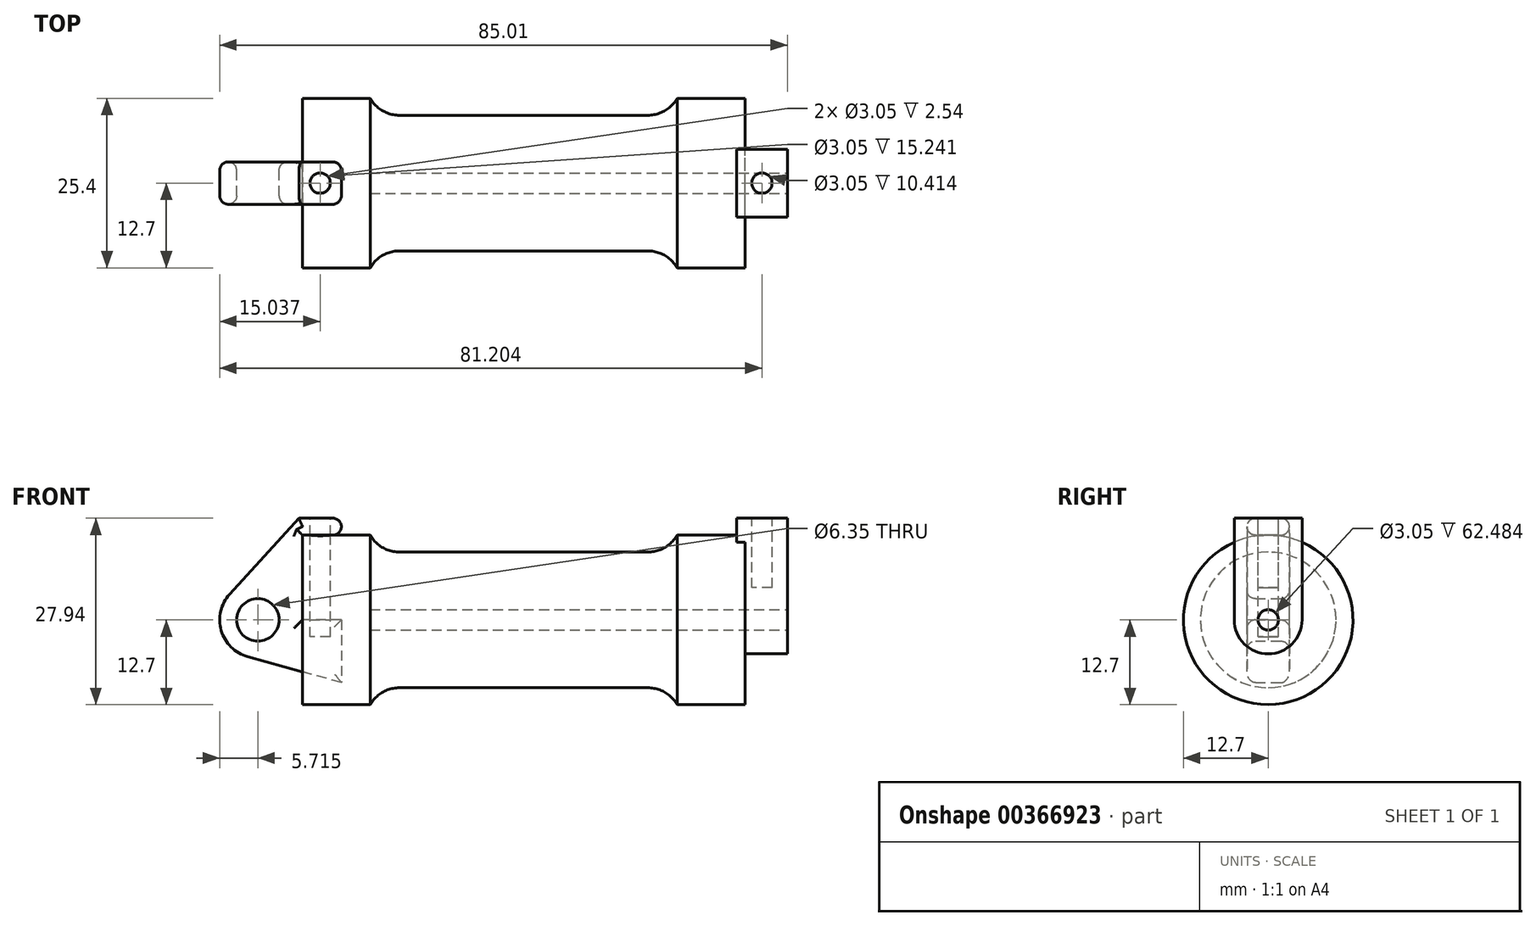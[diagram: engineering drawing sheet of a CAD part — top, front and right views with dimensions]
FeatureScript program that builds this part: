
annotation { "Feature Type Name" : "Feature", "Feature Type Description" : "" }
export const myFeature = defineFeature(function(context is Context, id is Id, definition is map)
    precondition{}
    {
        {
            var Q0;
            Q0=qCreatedBy(makeId("Front.planeOp"),FACE);
            var sketch = newSketch(context, id + "F0", { "sketchPlane" : qUnion([Q0])});
            skLineSegment(sketch, "E0", {"start": v(0, 0) * mm, "end": v(0, 12.7) * mm});
            skLineSegment(sketch, "E1", {"start": v(0, 12.7) * mm, "end": v(10.16, 12.7) * mm});
            skLineSegment(sketch, "E2", {"start": v(10.16, 12.7) * mm, "end": v(10.16, 10.16) * mm});
            skLineSegment(sketch, "E3", {"start": v(10.16, 10.16) * mm, "end": v(56.13, 10.16) * mm});
            skLineSegment(sketch, "E4", {"start": v(56.13, 10.16) * mm, "end": v(56.13, 12.7) * mm});
            skLineSegment(sketch, "E5", {"start": v(56.13, 12.7) * mm, "end": v(66.3, 12.7) * mm});
            skLineSegment(sketch, "E6", {"start": v(66.3, 12.7) * mm, "end": v(66.3, 0) * mm});
            skLineSegment(sketch, "E7", {"start": v(66.3, 0) * mm, "end": v(0, 0) * mm});
            skLineSegment(sketch, "E8", {"start": v(5.84, 15.24) * mm, "end": v(-0.5, 15.24) * mm});
            skLineSegment(sketch, "E9", {"start": v(-0.5, 15.24) * mm, "end": v(-10.88, 3.85) * mm});
            skLineSegment(sketch, "E10", {"start": v(0, 0) * mm, "end": v(-6.65, 0) * mm});
            skCircle(sketch, "E11", {"center": v(-6.65, 0) * mm, "radius": 5.72 * mm});
            skCircle(sketch, "E12", {"center": v(-6.65, 0) * mm, "radius": 3.18 * mm});
            skLineSegment(sketch, "E13", {"start": v(5.84, 15.24) * mm, "end": v(5.84, -9.4) * mm});
            skLineSegment(sketch, "E14", {"start": v(5.84, -9.4) * mm, "end": v(-8.18, -5.5) * mm});
            skSolve(sketch);
        }
        {
            var Q0;
            {var subQ0=sQuery(id+"F0.wireOp",EDGE,"E0");Q0=makeQuery(id+"F0.imprint","IMPRINT",FACE,{"disambiguationData":[TD([[makeQuery(id+"F0.imprint","IMPRINT",EDGE,{"derivedFrom":subQ0}),-1.0]])]});}
            var Q1;
            {var subQ0=sQuery(id+"F0.wireOp",EDGE,"E2");Q1=makeQuery(id+"F0.imprint","IMPRINT",FACE,{"disambiguationData":[TD([[makeQuery(id+"F0.imprint","IMPRINT",EDGE,{"derivedFrom":subQ0}),-1.0]])]});}
            var Q2;
            Q2=sQuery(id+"F0.wireOp",EDGE,"E7");
            revolve(context, id + "F1", {"entities" : qUnion([Q0, Q1]), "axis" : qUnion([Q2]), "revolveType" : RevolveType.FULL});
        }
        {
            var Q0;
            {var subQ1=sQuery(id+"F0.wireOp",EDGE,"E0");Q0=makeQuery(id+"F0.imprint","IMPRINT",FACE,{"disambiguationData":[TD([[makeQuery(id+"F0.imprint","IMPRINT",EDGE,{"derivedFrom":subQ1}),1.0]])]});}
            var Q1;
            {var subQ0=sQuery(id+"F0.wireOp",EDGE,"E14");Q1=makeQuery(id+"F0.imprint","IMPRINT",FACE,{"disambiguationData":[TD([[makeQuery(id+"F0.imprint","IMPRINT",EDGE,{"derivedFrom":subQ0}),-1.0]])]});}
            var Q2;
            {var subQ5=sQuery(id+"F0.wireOp",EDGE,"E12");Q2=makeQuery(id+"F0.imprint","IMPRINT",FACE,{"disambiguationData":[TD([[makeQuery(id+"F0.imprint","IMPRINT",EDGE,{"derivedFrom":subQ5}),-1.0]])]});}
            extrude(context, id + "F2", {"entities" : qUnion([Q0, Q1, Q2]), "endBound" : BoundingType.SYMMETRIC, "depth" : 6.35 * mm});
        }
        {
            var Q0;
            Q0=makeQuery(id+"F1.opRevolve","SWEPT_FACE",FACE,{"disambiguationData":[OSD([sQuery(id+"F0.wireOp",EDGE,"E6")])]});
            var sketch = newSketch(context, id + "F3", { "sketchPlane" : qUnion([Q0])});
            skCircle(sketch, "E15", {"center": v(0, 0) * mm, "radius": 1.52 * mm});
            skCircle(sketch, "E16", {"center": v(0, 0) * mm, "radius": 5.08 * mm});
            skLineSegment(sketch, "E17", {"start": v(5.08, 0) * mm, "end": v(5.08, 15.24) * mm});
            skLineSegment(sketch, "E18", {"start": v(-5.08, 0) * mm, "end": v(-5.08, 15.24) * mm});
            skLineSegment(sketch, "E19", {"start": v(-5.08, 15.24) * mm, "end": v(5.08, 15.24) * mm});
            skSolve(sketch);
        }
        {
            var Q0;
            Q0=makeQuery(id+"F3.imprint","IMPRINT",FACE,{"disambiguationData":[TD([[makeQuery(id+"F3.imprint","IMPRINT",EDGE,{"derivedFrom":sQuery(id+"F3.wireOp",EDGE,"E15")}),1.0]])]});
            var Q1;
            Q1=makeQuery(id+"F1.opRevolve","SWEPT_FACE",FACE,{"disambiguationData":[OSD([sQuery(id+"F0.wireOp",EDGE,"E2")])]});
            extrude(context, id + "F4", {"entities" : qUnion([Q0]), "operationType" : NewBodyOperationType.REMOVE, "endBound" : BoundingType.UP_TO_SURFACE, "oppositeDirection" : true, "endBoundEntityFace" : qUnion([Q1]), "depth" : 25.4 * mm});
        }
        {
            var Q0;
            {var subQ0=sQuery(id+"F3.wireOp",EDGE,"E17");var subQ1=sQuery(id+"F3.wireOp",EDGE,"E16");var subQ2=makeQuery(id+"F3.imprint","INTERSECT",VERTEX,{"derivedFrom":[subQ1,subQ0]});Q0=makeQuery(id+"F3.imprint","IMPRINT",FACE,{"disambiguationData":[TD([[makeQuery(id+"F3.imprint","IMPRINT",EDGE,{"disambiguationData":[TD([[subQ2,-1.0]])],"derivedFrom":subQ1}),-1.0]])]});}
            var Q1;
            Q1=makeQuery(id+"F3.imprint","IMPRINT",FACE,{"disambiguationData":[TD([[makeQuery(id+"F3.imprint","IMPRINT",EDGE,{"derivedFrom":sQuery(id+"F3.wireOp",EDGE,"E15")}),-1.0]])]});
            var Q2;
            {var subQ0=sQuery(id+"F3.wireOp",EDGE,"E19");Q2=makeQuery(id+"F3.imprint","IMPRINT",FACE,{"disambiguationData":[TD([[makeQuery(id+"F3.imprint","IMPRINT",EDGE,{"derivedFrom":subQ0}),-1.0]])]});}
            extrude(context, id + "F5", {"entities" : qUnion([Q0, Q1, Q2]), "operationType" : NewBodyOperationType.ADD, "oppositeDirection" : true, "depth" : 1.27 * mm});
        }
        {
            var Q0;
            {var subQ0=sQuery(id+"F3.wireOp",EDGE,"E17");var subQ1=sQuery(id+"F3.wireOp",EDGE,"E16");var subQ2=makeQuery(id+"F3.imprint","INTERSECT",VERTEX,{"derivedFrom":[subQ1,subQ0]});Q0=makeQuery(id+"F3.imprint","IMPRINT",FACE,{"disambiguationData":[TD([[makeQuery(id+"F3.imprint","IMPRINT",EDGE,{"disambiguationData":[TD([[subQ2,-1.0]])],"derivedFrom":subQ1}),-1.0]])]});}
            var Q1;
            {var subQ0=sQuery(id+"F3.wireOp",EDGE,"E19");Q1=makeQuery(id+"F3.imprint","IMPRINT",FACE,{"disambiguationData":[TD([[makeQuery(id+"F3.imprint","IMPRINT",EDGE,{"derivedFrom":subQ0}),-1.0]])]});}
            var Q2;
            Q2=makeQuery(id+"F3.imprint","IMPRINT",FACE,{"disambiguationData":[TD([[makeQuery(id+"F3.imprint","IMPRINT",EDGE,{"derivedFrom":sQuery(id+"F3.wireOp",EDGE,"E15")}),-1.0]])]});
            extrude(context, id + "F6", {"entities" : qUnion([Q0, Q1, Q2]), "operationType" : NewBodyOperationType.ADD, "depth" : 6.35 * mm});
        }
        {
            var Q0;
            {var subQ0=sQuery(id+"F3.wireOp",EDGE,"E19");Q0=makeQuery(id+"F6.boolean.opBoolean","MERGE",FACE,{"derivedFrom":[makeQuery(id+"F5.opExtrude","SWEPT_FACE",FACE,{"disambiguationData":[OSD([subQ0])]}),makeQuery(id+"F6.opExtrude","SWEPT_FACE",FACE,{"disambiguationData":[OSD([subQ0])]})]});}
            var sketch = newSketch(context, id + "F7", { "sketchPlane" : qUnion([Q0])});
            skCircle(sketch, "E20", {"center": v(2.67, 0) * mm, "radius": 1.52 * mm});
            skCircle(sketch, "E21", {"center": v(68.83, 0) * mm, "radius": 1.52 * mm});
            skLineSegment(sketch, "E22", {"start": v(65.02, 0) * mm, "end": v(72.64, 0) * mm, "construction": true});
            skSolve(sketch);
        }
        {
            var Q0;
            Q0=makeQuery(id+"F7.imprint","IMPRINT",FACE,{"disambiguationData":[TD([[makeQuery(id+"F7.imprint","IMPRINT",EDGE,{"derivedFrom":sQuery(id+"F7.wireOp",EDGE,"E20")}),1.0]])]});
            extrude(context, id + "F8", {"entities" : qUnion([Q0]), "operationType" : NewBodyOperationType.REMOVE, "oppositeDirection" : true, "depth" : 17.78 * mm});
        }
        {
            var Q0;
            Q0=makeQuery(id+"F7.imprint","IMPRINT",FACE,{"disambiguationData":[TD([[makeQuery(id+"F7.imprint","IMPRINT",EDGE,{"derivedFrom":sQuery(id+"F7.wireOp",EDGE,"E21")}),1.0]])]});
            extrude(context, id + "F9", {"entities" : qUnion([Q0]), "operationType" : NewBodyOperationType.REMOVE, "oppositeDirection" : true, "depth" : 10.4 * mm});
        }
        {
            var Q0;
            Q0=makeQuery(id+"F5.boolean.opBoolean","MERGE",FACE,{"derivedFrom":[makeQuery(id+"F1.opRevolve","SWEPT_FACE",FACE,{"disambiguationData":[OSD([sQuery(id+"F0.wireOp",EDGE,"E6")])]}),makeQuery(id+"F5.opExtrude","CAP_FACE",FACE,{"disambiguationData":[OSD([sQuery(id+"F3.wireOp",EDGE,"E15"),sQuery(id+"F3.wireOp",EDGE,"E16"),sQuery(id+"F3.wireOp",EDGE,"E17"),sQuery(id+"F3.wireOp",EDGE,"E18"),sQuery(id+"F3.wireOp",EDGE,"E19")])],"isStart":true})]});
            var Q1;
            Q1=makeQuery(id+"F1.opRevolve","SWEPT_EDGE",EDGE,{"disambiguationData":[OSD([sQuery(id+"F0.wireOp",EDGE,"E4"),sQuery(id+"F0.wireOp",EDGE,"E5")])]});
            var Q2;
            Q2=makeQuery(id+"F1.opRevolve","SWEPT_FACE",FACE,{"disambiguationData":[OSD([sQuery(id+"F0.wireOp",EDGE,"E2")])]});
            var Q3;
            Q3=makeQuery(id+"F6.opExtrude","CAP_FACE",FACE,{"disambiguationData":[OSD([sQuery(id+"F3.wireOp",EDGE,"E15"),sQuery(id+"F3.wireOp",EDGE,"E16"),sQuery(id+"F3.wireOp",EDGE,"E17"),sQuery(id+"F3.wireOp",EDGE,"E18"),sQuery(id+"F3.wireOp",EDGE,"E19")])],"isStart":false});
            var Q4;
            {var subQ0=sQuery(id+"F3.wireOp",EDGE,"E19");Q4=makeQuery(id+"F6.boolean.opBoolean","MERGE",FACE,{"derivedFrom":[makeQuery(id+"F5.opExtrude","SWEPT_FACE",FACE,{"disambiguationData":[OSD([subQ0])]}),makeQuery(id+"F6.opExtrude","SWEPT_FACE",FACE,{"disambiguationData":[OSD([subQ0])]})]});}
            var Q5;
            Q5=makeQuery(id+"F1.opRevolve","SWEPT_FACE",FACE,{"disambiguationData":[OSD([sQuery(id+"F0.wireOp",EDGE,"E0")])]});
            var Q6;
            Q6=makeQuery(id+"F2.opExtrude","CAP_FACE",FACE,{"disambiguationData":[OSD([sQuery(id+"F0.wireOp",EDGE,"E0"),sQuery(id+"F0.wireOp",EDGE,"E1"),sQuery(id+"F0.wireOp",EDGE,"E7"),sQuery(id+"F0.wireOp",EDGE,"E8"),sQuery(id+"F0.wireOp",EDGE,"E9"),sQuery(id+"F0.wireOp",EDGE,"E11"),sQuery(id+"F0.wireOp",EDGE,"E12"),sQuery(id+"F0.wireOp",EDGE,"E13"),sQuery(id+"F0.wireOp",EDGE,"E14")])],"isStart":false});
            var Q7;
            Q7=makeQuery(id+"F2.opExtrude","CAP_FACE",FACE,{"disambiguationData":[OSD([sQuery(id+"F0.wireOp",EDGE,"E0"),sQuery(id+"F0.wireOp",EDGE,"E1"),sQuery(id+"F0.wireOp",EDGE,"E7"),sQuery(id+"F0.wireOp",EDGE,"E8"),sQuery(id+"F0.wireOp",EDGE,"E9"),sQuery(id+"F0.wireOp",EDGE,"E11"),sQuery(id+"F0.wireOp",EDGE,"E12"),sQuery(id+"F0.wireOp",EDGE,"E13"),sQuery(id+"F0.wireOp",EDGE,"E14")])],"isStart":true});
            var Q8;
            {var subQ0=sQuery(id+"F0.wireOp",EDGE,"E13");Q8=makeQuery(id+"F2.opExtrude","SWEPT_FACE",FACE,{"disambiguationData":[OSD([subQ0]),TDD([makeQuery(id+"F0.imprint","IMPRINT",EDGE,{"disambiguationData":[TD([[makeQuery(id+"F0.imprint","INTERSECT",VERTEX,{"derivedFrom":[sQuery(id+"F0.wireOp",EDGE,"E8"),subQ0]}),-1.0]])],"derivedFrom":subQ0})])]});}
            fillet(context, id + "F10", {"entities" : qUnion([Q0, Q1, Q2, Q3, Q4, Q5, Q6, Q7, Q8]), "radius" : 1.27 * mm, "tangentPropagation" : true, "allowEdgeOverflow" : false});
        }
        {
            var Q0;
            Q0=makeQuery(id+"F1.opRevolve","SWEPT_FACE",FACE,{"disambiguationData":[OSD([sQuery(id+"F0.wireOp",EDGE,"E3")])]});
            var Q1;
            {var subQ0=sQuery(id+"F0.wireOp",EDGE,"E4");Q1=makeQuery(id+"F10.opFillet","BLEND_EDGE",EDGE,{"blendedFrom":[makeQuery(id+"F1.opRevolve","SWEPT_EDGE",EDGE,{"disambiguationData":[OSD([subQ0,sQuery(id+"F0.wireOp",EDGE,"E5")])]}),makeQuery(id+"F1.opRevolve","SWEPT_FACE",FACE,{"disambiguationData":[OSD([subQ0])]})],"blendedInto":[makeQuery(id+"F1.opRevolve","SWEPT_FACE",FACE,{"disambiguationData":[OSD([subQ0])]})]});}
            fillet(context, id + "F11", {"entities" : qUnion([Q0, Q1]), "radius" : 5.08 * mm, "tangentPropagation" : true, "allowEdgeOverflow" : false});
        }
    });
